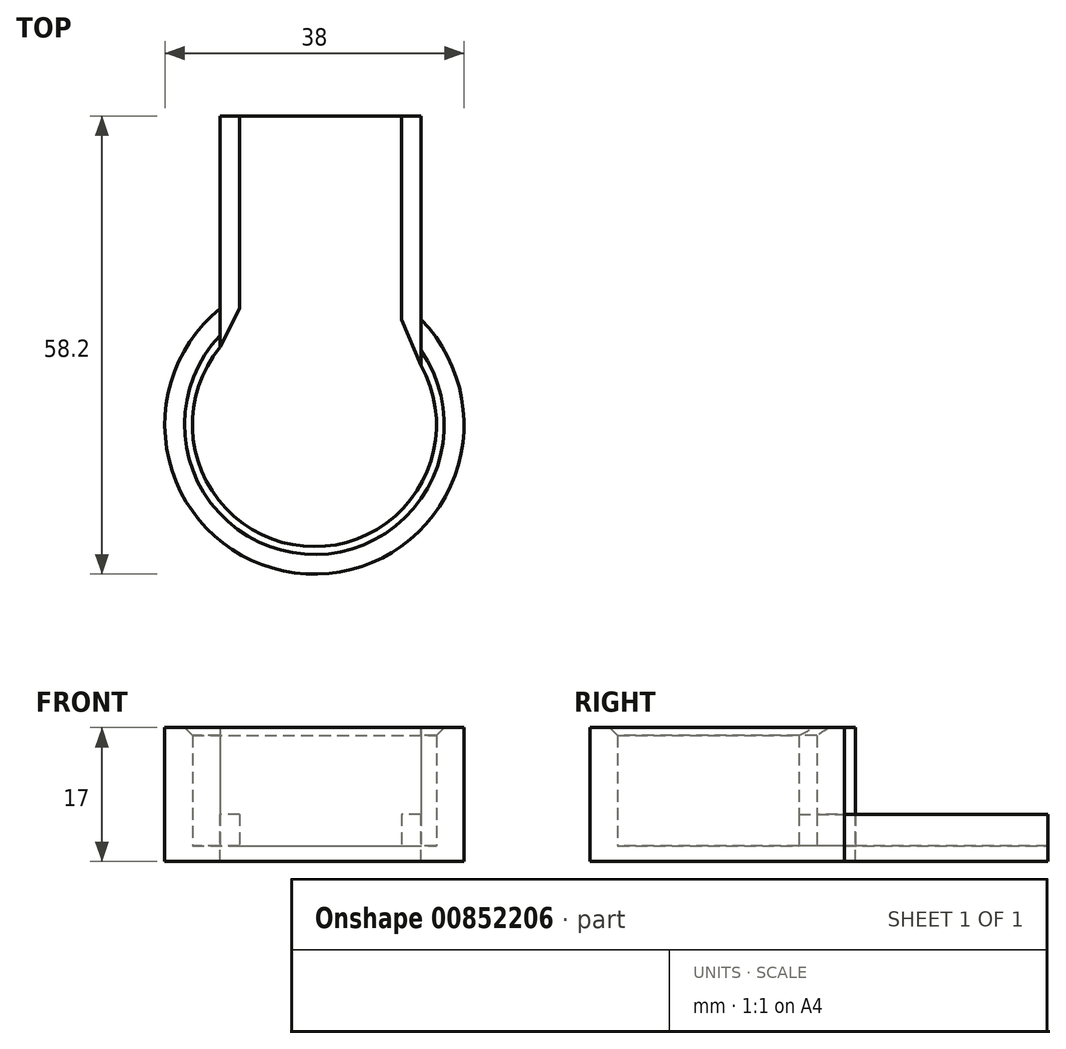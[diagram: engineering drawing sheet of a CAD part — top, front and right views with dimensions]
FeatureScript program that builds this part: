
annotation { "Feature Type Name" : "Feature", "Feature Type Description" : "" }
export const myFeature = defineFeature(function(context is Context, id is Id, definition is map)
    precondition{}
    {
        {
            var Q0;
            Q0=qCreatedBy(makeId("Top.planeOp"),FACE);
            var sketch = newSketch(context, id + "F0", { "sketchPlane" : qUnion([Q0])});
            skArc(sketch, "E0", {"start": v(-41.92, 21.04) * mm, "mid": v(-31.33, -4.23) * mm, "end": v(-16.4, 18.74) * mm});
            skArc(sketch, "E1.0", {"start": v(-41.92, 25.95) * mm, "mid": v(-31, -7.76) * mm, "end": v(-16.4, 24.53) * mm});
            skLineSegment(sketch, "E2.bottom", {"start": v(-29.94, 11.2) * mm, "end": v(-29.94, 11.2) * mm});
            skLineSegment(sketch, "E2.top", {"start": v(-29.94, 11.2) * mm, "end": v(-29.94, 11.2) * mm});
            skLineSegment(sketch, "E2.left", {"start": v(-29.94, 11.2) * mm, "end": v(-29.94, 11.2) * mm});
            skLineSegment(sketch, "E2.right", {"start": v(-29.94, 11.2) * mm, "end": v(-29.94, 11.2) * mm});
            skLineSegment(sketch, "E3.bottom", {"start": v(-41.92, 50.4) * mm, "end": v(-16.4, 50.4) * mm});
            skLineSegment(sketch, "E3.left", {"start": v(-41.92, 50.4) * mm, "end": v(-41.92, 21.04) * mm});
            skLineSegment(sketch, "E3.right", {"start": v(-16.4, 50.4) * mm, "end": v(-16.4, 18.74) * mm});
            skSolve(sketch);
        }
        {
            var Q0;
            {var subQ1=sQuery(id+"F0.wireOp",EDGE,"E0");Q0=makeQuery(id+"F0.imprint","IMPRINT",FACE,{"disambiguationData":[TD([[makeQuery(id+"F0.imprint","IMPRINT",EDGE,{"derivedFrom":subQ1}),1.0]])]});}
            var Q1;
            {var subQ0=sQuery(id+"F0.wireOp",EDGE,"E0");Q1=makeQuery(id+"F0.imprint","IMPRINT",FACE,{"disambiguationData":[TD([[makeQuery(id+"F0.imprint","IMPRINT",EDGE,{"derivedFrom":subQ0}),-1.0]])]});}
            extrude(context, id + "F1", {"entities" : qUnion([Q0, Q1]), "oppositeDirection" : true, "depth" : 2 * mm, "offsetDistance" : 25 * mm});
        }
        {
            var Q0;
            {var subQ0=sQuery(id+"F0.wireOp",EDGE,"E0");Q0=makeQuery(id+"F0.imprint","IMPRINT",FACE,{"disambiguationData":[TD([[makeQuery(id+"F0.imprint","IMPRINT",EDGE,{"derivedFrom":subQ0}),-1.0]])]});}
            extrude(context, id + "F2", {"entities" : qUnion([Q0]), "operationType" : NewBodyOperationType.ADD, "depth" : 15 * mm, "offsetDistance" : 25 * mm});
        }
        {
            var Q0;
            Q0=qCreatedBy(makeId("Top.planeOp"),FACE);
            var sketch = newSketch(context, id + "F3", { "sketchPlane" : qUnion([Q0])});
            skLineSegment(sketch, "E4.0.0", {"start": v(-16.4, 50.4) * mm, "end": v(-41.92, 50.4) * mm});
            skLineSegment(sketch, "E4.0.1", {"start": v(-41.92, 50.4) * mm, "end": v(-41.92, 25.95) * mm});
            skLineSegment(sketch, "E4.0.2", {"start": v(-41.92, 25.95) * mm, "end": v(-41.92, 21.04) * mm});
            skArc(sketch, "E4.0.3", {"start": v(-41.92, 21.04) * mm, "mid": v(-31.33, -4.23) * mm, "end": v(-16.4, 18.74) * mm});
            skLineSegment(sketch, "E4.0.4", {"start": v(-16.4, 18.74) * mm, "end": v(-16.4, 24.53) * mm});
            skLineSegment(sketch, "E4.0.5", {"start": v(-16.4, 24.53) * mm, "end": v(-16.4, 50.4) * mm});
            skLineSegment(sketch, "E5.0", {"start": v(-39.42, 47.9) * mm, "end": v(-39.42, 25.95) * mm});
            skLineSegment(sketch, "E5.2", {"start": v(-18.9, 24.53) * mm, "end": v(-18.9, 47.9) * mm});
            skLineSegment(sketch, "E6", {"start": v(-39.42, 25.95) * mm, "end": v(-41.92, 21.04) * mm});
            skLineSegment(sketch, "E7", {"start": v(-18.9, 24.53) * mm, "end": v(-16.4, 18.74) * mm});
            skLineSegment(sketch, "E8", {"start": v(-39.42, 47.9) * mm, "end": v(-39.42, 50.4) * mm});
            skLineSegment(sketch, "E9", {"start": v(-18.9, 47.9) * mm, "end": v(-18.9, 50.4) * mm});
            skSolve(sketch);
        }
        {
            var Q0;
            {var subQ0=sQuery(id+"F3.wireOp",EDGE,"E4.0.1");Q0=makeQuery(id+"F3.imprint","IMPRINT",FACE,{"disambiguationData":[TD([[makeQuery(id+"F3.imprint","IMPRINT",EDGE,{"derivedFrom":subQ0}),1.0]])]});}
            var Q1;
            Q1=makeQuery(id+"F3.imprint","IMPRINT",FACE,{"disambiguationData":[TD([[makeQuery(id+"F3.imprint","IMPRINT",EDGE,{"derivedFrom":sQuery(id+"F3.wireOp",EDGE,"E4.0.4")}),1.0]])]});
            extrude(context, id + "F4", {"entities" : qUnion([Q0, Q1]), "operationType" : NewBodyOperationType.ADD, "depth" : 4 * mm, "offsetDistance" : 25 * mm});
        }
        {
            var Q0;
            Q0=makeQuery(id+"F2.opExtrude","CAP_EDGE",EDGE,{"disambiguationData":[OSD([sQuery(id+"F0.wireOp",EDGE,"E0")])],"isStart":false});
            chamfer(context, id + "F5", {"entities" : qUnion([Q0]), "width" : 1 * mm, "tangentPropagation" : true});
        }
    });
